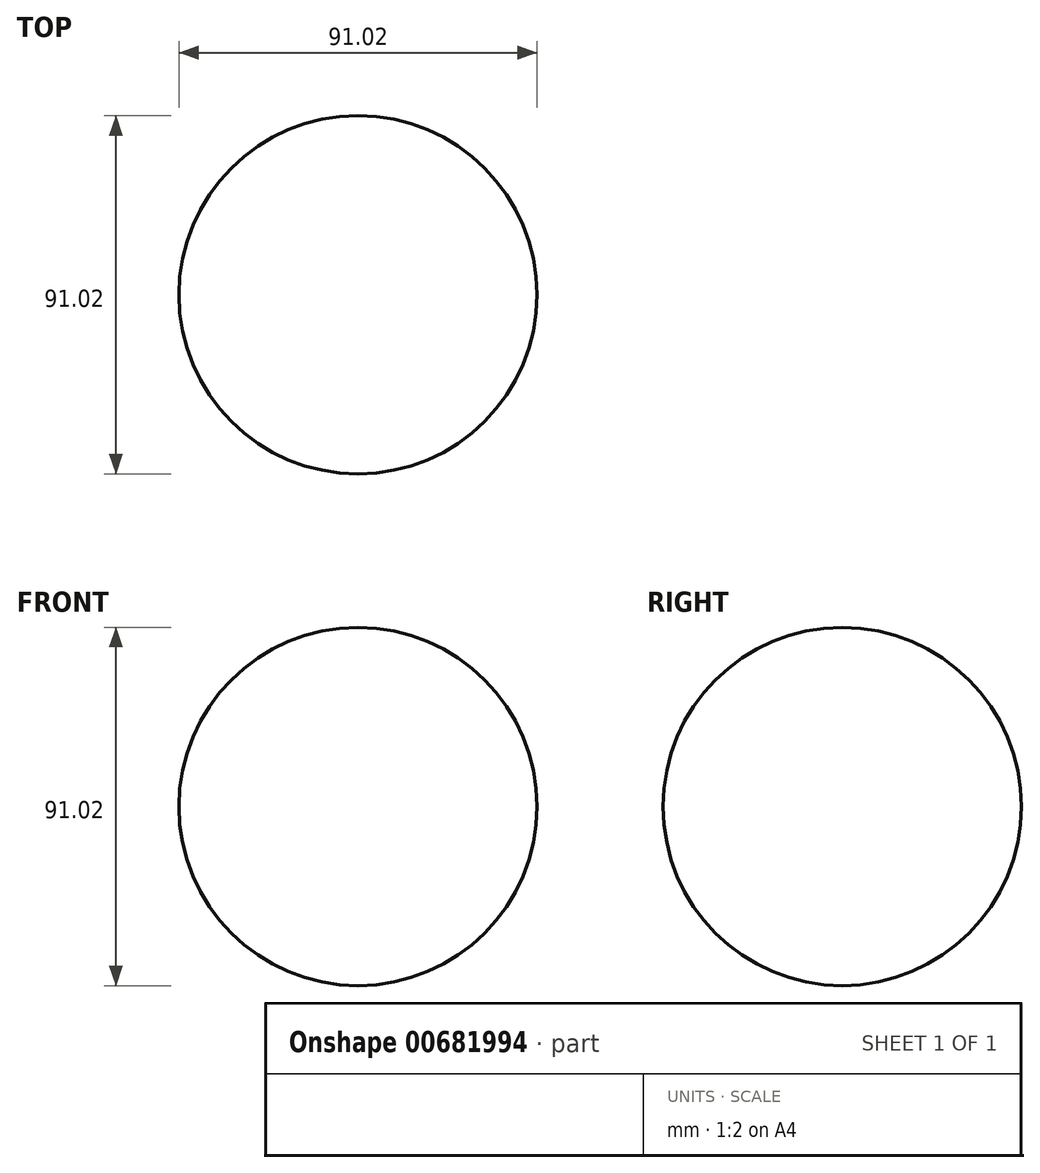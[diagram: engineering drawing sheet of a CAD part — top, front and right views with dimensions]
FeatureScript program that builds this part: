
annotation { "Feature Type Name" : "Feature", "Feature Type Description" : "" }
export const myFeature = defineFeature(function(context is Context, id is Id, definition is map)
    precondition{}
    {
        {
            var Q0;
            Q0=qCreatedBy(makeId("Front.planeOp"),FACE);
            var sketch = newSketch(context, id + "F0", { "sketchPlane" : qUnion([Q0])});
            skLineSegment(sketch, "E0", {"start": v(0, 45.5) * mm, "end": v(0, -45.5) * mm});
            skArc(sketch, "E1", {"start": v(0, 45.5) * mm, "mid": v(-45.5, 0) * mm, "end": v(0, -45.5) * mm});
            skSolve(sketch);
        }
        {
            var Q0;
            Q0=makeQuery(id+"F0.imprint","IMPRINT",FACE,{"disambiguationData":[TD([[makeQuery(id+"F0.imprint","IMPRINT",EDGE,{"derivedFrom":sQuery(id+"F0.wireOp",EDGE,"E0")}),-1.0]])]});
            var Q1;
            Q1=sQuery(id+"F0.wireOp",EDGE,"E0");
            revolve(context, id + "F1", {"entities" : qUnion([Q0]), "axis" : qUnion([Q1]), "revolveType" : RevolveType.FULL});
        }
    });
